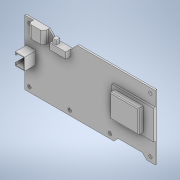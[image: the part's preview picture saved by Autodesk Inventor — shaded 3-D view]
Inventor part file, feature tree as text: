
AUTODESK INVENTOR PART (.ipt)
format: ipt  version: 2021 (Build 250183000, 183)  size: 298,496 bytes
history: native  units: mm
features: sketch x14, extrude x12, fillet x3, chamfer x2, hole x2
ambient origin geometry x8: Origin, YZ Plane, XZ Plane, XY Plane, X Axis, Y Axis, Z Axis, Center Point
bodies: Solid1 (feature_tree)
feature tree (33):
  extrude  "Extrusion1"  Depth=40.0mm
  extrude  "Extrusion2"  Depth=1.0mm
  chamfer  "Chamfer1"  Distance=1.0mm
  extrude  "Extrusion3"  Depth=28.8mm
  fillet  "Fillet1"  Radius=3.9mm
  extrude  "Extrusion4"  Depth=2.0mm TaperAngle=45.0deg
  extrude  "Extrusion5"  Depth=14.73mm
  hole  "Hole1"  [1 undecoded]
  hole  "Hole2"  [1 undecoded]
  extrude  "Extrusion6"  Depth=3.2mm TaperAngle=0.0deg
  chamfer  "Chamfer2"  Distance=2.8mm
  extrude  "Extrusion7"  Depth=3.0mm
  extrude  "Extrusion8"  Depth=2.2mm
  extrude  "Extrusion9"  Depth=3.0mm
  extrude  "Extrusion10"  Depth=3.0mm
  fillet  "Fillet2"  Radius=3.0mm
  extrude  "Extrusion11"  Depth=3.0mm
  fillet  "Fillet3"  Radius=3.0mm
  extrude  "Extrusion12"  Depth=37.0mm
  sketch  "Sketch1"  dims[d0=81.0mm d1=40.0mm]
  sketch  "Sketch2"  dims[d2=20.0mm d3=40.5mm d4=1.0mm d5=0.0mm]
  sketch  "Sketch3"  dims[d6=18.7mm d7=28.8mm d8=3.9mm]
  sketch  "Sketch4"  dims[d9=1.0mm d10=0.0mm d11=3.88mm d12=2.0mm d13=45.0deg]
  sketch  "Sketch5"  dims[d14=5.46mm d15=14.73mm]
  sketch  "Sketch6"  dims[d16=7.62mm d17=3.2mm d18=0.0mm]
  sketch  "Sketch7"  dims[d19=2.0mm d20=3.8mm]
  sketch  "Sketch8"  dims[d21=10.0mm d22=3.2mm d23=0.0mm]
  sketch  "Sketch9"  dims[d24=0.6mm]
  sketch  "Sketch10"  dims[d25=1.2mm]
  sketch  "Sketch11"  dims[d26=2.4mm]
  sketch  "Sketch12"  dims[d27=2.2mm d28=2.8mm d29=0.0mm]
  sketch  "Sketch13"  dims[d30=3.0mm d31=28.0mm]
  sketch  "Sketch14"  dims[d32=53.0mm d33=78.0mm d34=3.0mm d35=3.0mm d36=3.0mm d37=3.0mm d38=2.0mm d39=6.0mm d40=4.0mm d41=2.0mm d42=90.0deg d43=4.0mm d44=20.594885mm d45=3.0mm d46=37.0mm d47=78.0mm d48=37.0mm d49=2.0mm d50=6.0mm d51=4.0mm d52=2.0mm d53=90.0deg d54=4.0mm d55=20.594885mm d56=58.0mm d57=73.0mm d58=2.7mm d59=2.0mm d60=0.0mm d61=2.7mm d62=2.0mm d63=45.0deg d64=1.14mm d65=7.0mm d66=16.9mm d67=24.4mm d68=0.5mm d69=0.5mm d70=0.5mm d71=0.5mm d72=1.2mm d73=1.2mm d74=7.0mm d75=0.0mm d76=5.0mm d77=0.0mm d78=55.0mm d79=9.0mm d80=18.2mm d81=1.0mm d82=0.0mm d83=2.0mm d84=2.0mm d85=2.0mm d86=6.5mm d87=3.0mm d88=0.0mm d89=0.5mm d90=36.1mm d91=44.9mm d92=0.6mm d93=3.9mm d94=6.0mm d95=0.0mm d96=1.28mm d97=57.8mm d98=73.0mm d99=15.0mm d100=2.2mm d101=0.0mm]
note: 2 required parameter values undecoded (feature->parameter linkage not recoverable at this tier; creation-order binding heuristic only, values carry confidence <= 0.55)
